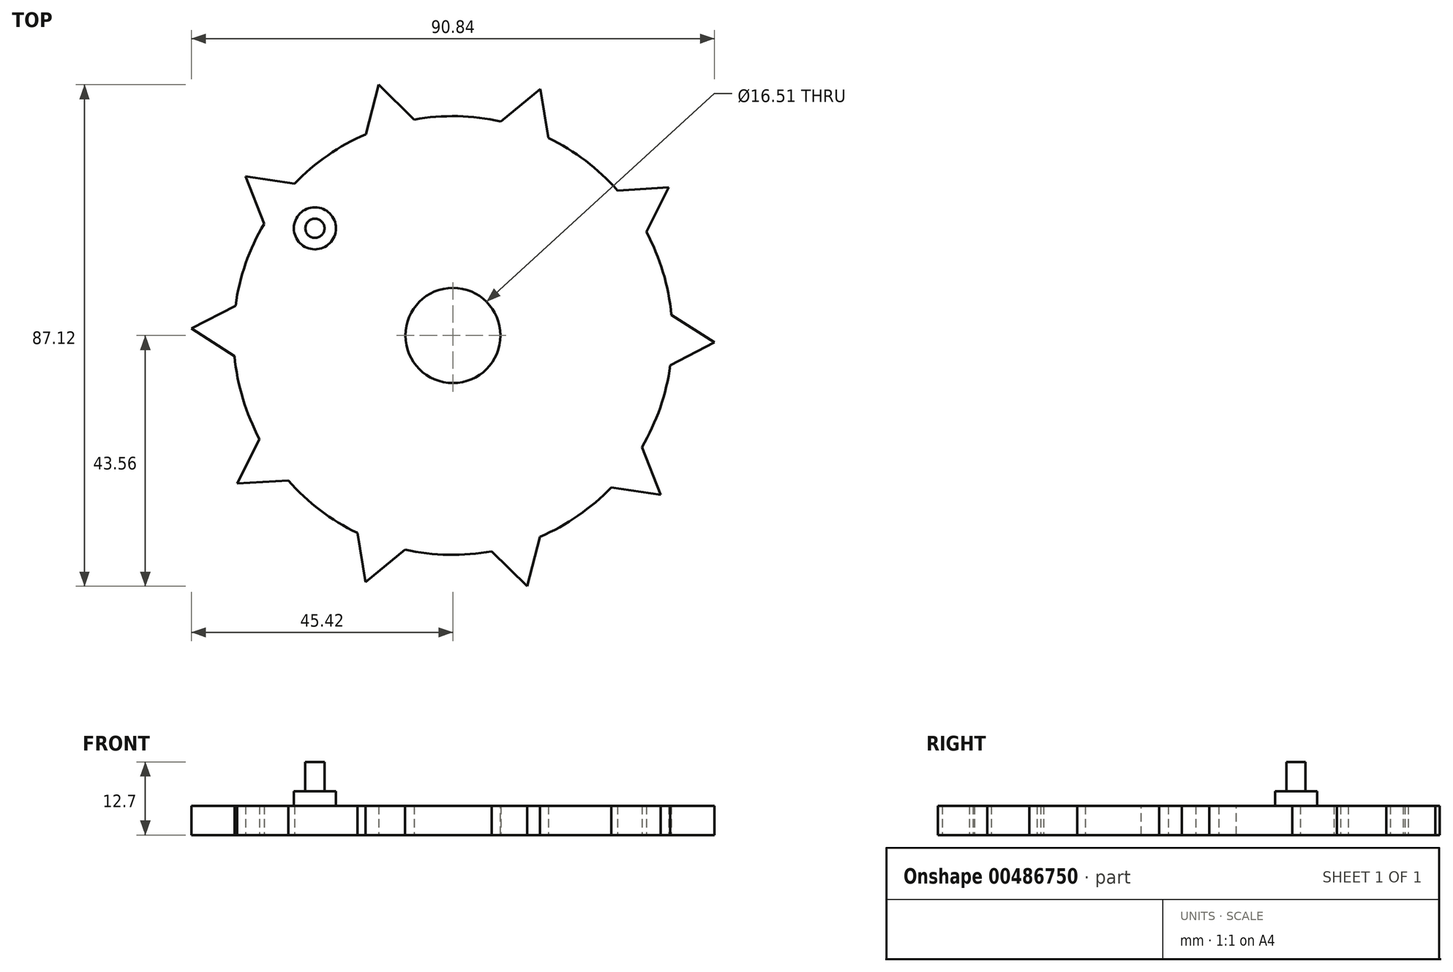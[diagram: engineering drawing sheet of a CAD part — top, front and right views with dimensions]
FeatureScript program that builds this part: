
annotation { "Feature Type Name" : "Feature", "Feature Type Description" : "" }
export const myFeature = defineFeature(function(context is Context, id is Id, definition is map)
    precondition{}
    {
        {
            var Q0;
            Q0=qCreatedBy(makeId("Top.planeOp"),FACE);
            var sketch = newSketch(context, id + "F0", { "sketchPlane" : qUnion([Q0])});
            skCircle(sketch, "E0", {"center": v(0, 0) * mm, "radius": 38.1 * mm});
            skCircle(sketch, "E1.cCircle", {"center": v(-30.3, 23.1) * mm, "radius": 3.67 * mm, "construction": true});
            skLineSegment(sketch, "E1.0", {"start": v(-31.4, 15.84) * mm, "end": v(-36.04, 27.66) * mm});
            skLineSegment(sketch, "E1.1", {"start": v(-36.04, 27.66) * mm, "end": v(-23.48, 25.77) * mm});
            skLineSegment(sketch, "E1.2", {"start": v(-23.48, 25.77) * mm, "end": v(-31.4, 15.84) * mm});
            skPoint(sketch, "E1.0.midPoint", {"position": v(-33.72, 21.75) * mm});
            skLineSegment(sketch, "E2.1.0", {"start": v(-45.42, 1.2) * mm, "end": v(-34.14, 7.05) * mm});
            skLineSegment(sketch, "E2.1.1", {"start": v(-34.71, -5.64) * mm, "end": v(-45.42, 1.2) * mm});
            skLineSegment(sketch, "E2.1.2", {"start": v(-34.14, 7.05) * mm, "end": v(-34.71, -5.64) * mm});
            skLineSegment(sketch, "E2.2.0", {"start": v(-37.45, -25.73) * mm, "end": v(-31.76, -14.37) * mm});
            skLineSegment(sketch, "E2.2.1", {"start": v(-24.77, -24.97) * mm, "end": v(-37.45, -25.73) * mm});
            skLineSegment(sketch, "E2.2.2", {"start": v(-31.76, -14.37) * mm, "end": v(-24.77, -24.97) * mm});
            skLineSegment(sketch, "E2.3.0", {"start": v(-15.17, -42.82) * mm, "end": v(-17.25, -30.3) * mm});
            skLineSegment(sketch, "E2.3.1", {"start": v(-5.36, -34.76) * mm, "end": v(-15.17, -42.82) * mm});
            skLineSegment(sketch, "E2.3.2", {"start": v(-17.25, -30.3) * mm, "end": v(-5.36, -34.76) * mm});
            skLineSegment(sketch, "E2.4.0", {"start": v(12.9, -43.56) * mm, "end": v(3.85, -34.65) * mm});
            skLineSegment(sketch, "E2.4.1", {"start": v(16.1, -31.27) * mm, "end": v(12.9, -43.56) * mm});
            skLineSegment(sketch, "E2.4.2", {"start": v(3.85, -34.65) * mm, "end": v(16.1, -31.27) * mm});
            skLineSegment(sketch, "E2.5.0", {"start": v(36.04, -27.66) * mm, "end": v(23.48, -25.77) * mm});
            skLineSegment(sketch, "E2.5.1", {"start": v(31.4, -15.84) * mm, "end": v(36.04, -27.66) * mm});
            skLineSegment(sketch, "E2.5.2", {"start": v(23.48, -25.77) * mm, "end": v(31.4, -15.84) * mm});
            skLineSegment(sketch, "E2.6.0", {"start": v(45.42, -1.2) * mm, "end": v(34.14, -7.05) * mm});
            skLineSegment(sketch, "E2.6.1", {"start": v(34.71, 5.64) * mm, "end": v(45.42, -1.2) * mm});
            skLineSegment(sketch, "E2.6.2", {"start": v(34.14, -7.05) * mm, "end": v(34.71, 5.64) * mm});
            skLineSegment(sketch, "E2.7.0", {"start": v(37.45, 25.73) * mm, "end": v(31.76, 14.37) * mm});
            skLineSegment(sketch, "E2.7.1", {"start": v(24.77, 24.97) * mm, "end": v(37.45, 25.73) * mm});
            skLineSegment(sketch, "E2.7.2", {"start": v(31.76, 14.37) * mm, "end": v(24.77, 24.97) * mm});
            skLineSegment(sketch, "E2.8.0", {"start": v(15.17, 42.82) * mm, "end": v(17.25, 30.3) * mm});
            skLineSegment(sketch, "E2.8.1", {"start": v(5.36, 34.76) * mm, "end": v(15.17, 42.82) * mm});
            skLineSegment(sketch, "E2.8.2", {"start": v(17.25, 30.3) * mm, "end": v(5.36, 34.76) * mm});
            skLineSegment(sketch, "E2.9.0", {"start": v(-12.9, 43.56) * mm, "end": v(-3.85, 34.65) * mm});
            skLineSegment(sketch, "E2.9.1", {"start": v(-16.1, 31.27) * mm, "end": v(-12.9, 43.56) * mm});
            skLineSegment(sketch, "E2.9.2", {"start": v(-3.85, 34.65) * mm, "end": v(-16.1, 31.27) * mm});
            skSolve(sketch);
        }
        {
            var Q0;
            Q0 = qSketchRegion(id + "F0", true);
            extrude(context, id + "F1", {"entities" : qUnion([Q0]), "depth" : 5.08 * mm, "offsetDistance" : 25.4 * mm});
        }
        {
            var Q0;
            Q0=makeQuery(id+"F1.opExtrude","CAP_FACE",FACE,{"disambiguationData":[OSD([sQuery(id+"F0.wireOp",EDGE,"E0"),sQuery(id+"F0.wireOp",EDGE,"E1.0"),sQuery(id+"F0.wireOp",EDGE,"E1.1"),sQuery(id+"F0.wireOp",EDGE,"E2.1.0"),sQuery(id+"F0.wireOp",EDGE,"E2.1.1"),sQuery(id+"F0.wireOp",EDGE,"E2.2.0"),sQuery(id+"F0.wireOp",EDGE,"E2.2.1"),sQuery(id+"F0.wireOp",EDGE,"E2.3.0"),sQuery(id+"F0.wireOp",EDGE,"E2.3.1"),sQuery(id+"F0.wireOp",EDGE,"E2.4.0"),sQuery(id+"F0.wireOp",EDGE,"E2.4.1"),sQuery(id+"F0.wireOp",EDGE,"E2.5.0"),sQuery(id+"F0.wireOp",EDGE,"E2.5.1"),sQuery(id+"F0.wireOp",EDGE,"E2.6.0"),sQuery(id+"F0.wireOp",EDGE,"E2.6.1"),sQuery(id+"F0.wireOp",EDGE,"E2.7.0"),sQuery(id+"F0.wireOp",EDGE,"E2.7.1"),sQuery(id+"F0.wireOp",EDGE,"E2.8.0"),sQuery(id+"F0.wireOp",EDGE,"E2.8.1"),sQuery(id+"F0.wireOp",EDGE,"E2.9.0"),sQuery(id+"F0.wireOp",EDGE,"E2.9.1")])],"isStart":false});
            var sketch = newSketch(context, id + "F2", { "sketchPlane" : qUnion([Q0])});
            skCircle(sketch, "E3", {"center": v(-23.96, 18.62) * mm, "radius": 3.65 * mm});
            skSolve(sketch);
        }
        {
            var Q0;
            Q0 = qSketchRegion(id + "F2", true);
            extrude(context, id + "F3", {"entities" : qUnion([Q0]), "operationType" : NewBodyOperationType.ADD, "depth" : 2.54 * mm, "offsetDistance" : 25.4 * mm});
        }
        {
            var Q0;
            Q0=makeQuery(id+"F3.opExtrude","CAP_FACE",FACE,{"disambiguationData":[OSD([sQuery(id+"F2.wireOp",EDGE,"E3")])],"isStart":false});
            var sketch = newSketch(context, id + "F4", { "sketchPlane" : qUnion([Q0])});
            skCircle(sketch, "E4", {"center": v(-23.96, 18.62) * mm, "radius": 1.67 * mm});
            skSolve(sketch);
        }
        {
            var Q0;
            Q0 = qSketchRegion(id + "F4", true);
            extrude(context, id + "F5", {"entities" : qUnion([Q0]), "operationType" : NewBodyOperationType.ADD, "depth" : 5.08 * mm, "offsetDistance" : 25.4 * mm});
        }
        {
            var Q0;
            Q0=makeQuery(id+"F1.opExtrude","CAP_FACE",FACE,{"disambiguationData":[OSD([sQuery(id+"F0.wireOp",EDGE,"E0"),sQuery(id+"F0.wireOp",EDGE,"E1.0"),sQuery(id+"F0.wireOp",EDGE,"E1.1"),sQuery(id+"F0.wireOp",EDGE,"E2.1.0"),sQuery(id+"F0.wireOp",EDGE,"E2.1.1"),sQuery(id+"F0.wireOp",EDGE,"E2.2.0"),sQuery(id+"F0.wireOp",EDGE,"E2.2.1"),sQuery(id+"F0.wireOp",EDGE,"E2.3.0"),sQuery(id+"F0.wireOp",EDGE,"E2.3.1"),sQuery(id+"F0.wireOp",EDGE,"E2.4.0"),sQuery(id+"F0.wireOp",EDGE,"E2.4.1"),sQuery(id+"F0.wireOp",EDGE,"E2.5.0"),sQuery(id+"F0.wireOp",EDGE,"E2.5.1"),sQuery(id+"F0.wireOp",EDGE,"E2.6.0"),sQuery(id+"F0.wireOp",EDGE,"E2.6.1"),sQuery(id+"F0.wireOp",EDGE,"E2.7.0"),sQuery(id+"F0.wireOp",EDGE,"E2.7.1"),sQuery(id+"F0.wireOp",EDGE,"E2.8.0"),sQuery(id+"F0.wireOp",EDGE,"E2.8.1"),sQuery(id+"F0.wireOp",EDGE,"E2.9.0"),sQuery(id+"F0.wireOp",EDGE,"E2.9.1")])],"isStart":false});
            var sketch = newSketch(context, id + "F6", { "sketchPlane" : qUnion([Q0])});
            skCircle(sketch, "E5", {"center": v(0, 0) * mm, "radius": 8.26 * mm});
            skSolve(sketch);
        }
        {
            var Q0;
            Q0 = qSketchRegion(id + "F6", true);
            extrude(context, id + "F7", {"entities" : qUnion([Q0]), "operationType" : NewBodyOperationType.REMOVE, "oppositeDirection" : true, "depth" : 25.4 * mm, "offsetDistance" : 25.4 * mm});
        }
    });
